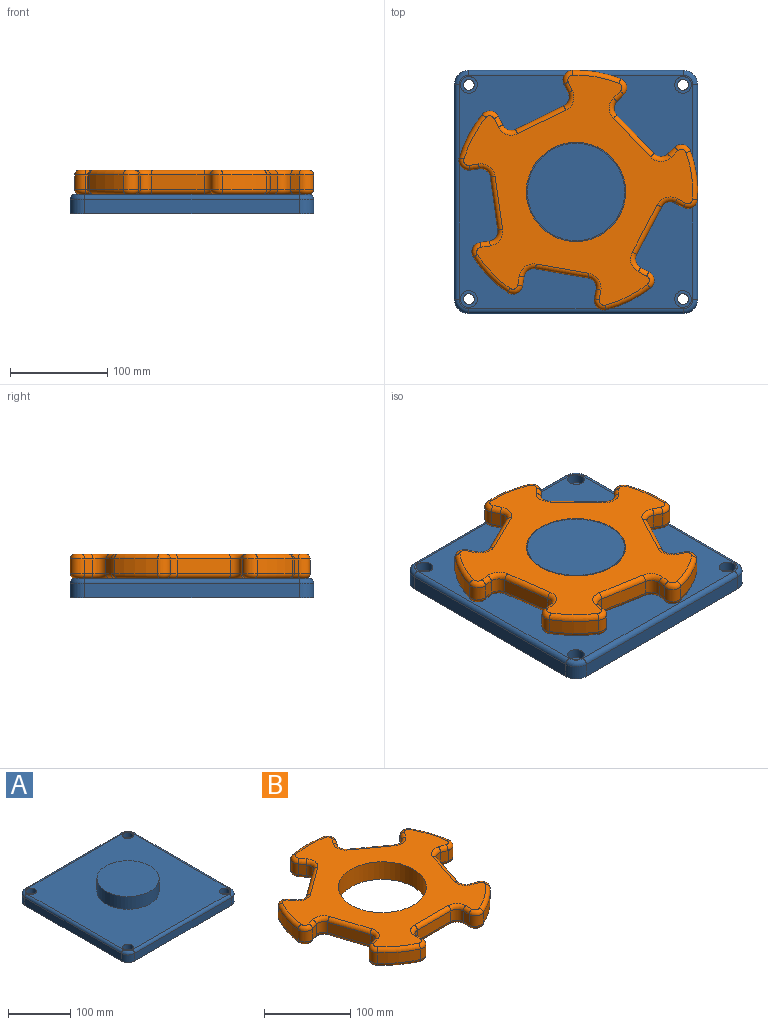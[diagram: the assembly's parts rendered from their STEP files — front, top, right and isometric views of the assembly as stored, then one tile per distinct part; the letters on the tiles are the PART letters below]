
ASSEMBLY  parts=2 mates=1
PART A: 32 faces, bbox 252.5x252.5x45 mm
  f0: plane 220x15mm, normal (1,0,0), area 3300mm2, adj f5,f8,f11,f27
  f1: plane 220x15mm, normal (0,1,0), area 3300mm2, adj f5,f8,f9,f31
  f2: plane 220x15mm, normal (-1,0,0), area 3300mm2, adj f5,f9,f10,f28
  f3: plane 220x15mm, normal (0,-1,0), area 3300mm2, adj f5,f10,f11,f24
  f4: plane 240x240mm, normal (0,0,1), area 48725.4mm2, adj f6,f14,f17,f20,f23,f24,f25,f26
  f5: plane 250x250mm, normal (0,0,-1), area 61926.7mm2, adj f0,f1,f2,f3,f8,f9,f10,f11
  f6: cylinder r=50mm len=100mm, axis (0,0,-1), area 7854mm2, adj f4,f7
  f7: plane 100x100mm, normal (0,0,1), area 7854mm2, adj f6
  f8: cylinder r=15mm len=15mm, axis (0,0,-1), area 353.4mm2, adj f0,f1,f5,f29
  f9: cylinder r=15mm len=15mm, axis (0,0,1), area 353.4mm2, adj f1,f2,f5,f30
  f10: cylinder r=15mm len=15mm, axis (0,0,-1), area 353.4mm2, adj f2,f3,f5,f26
  f11: cylinder r=15mm len=15mm, axis (0,0,1), area 353.4mm2, adj f0,f3,f5,f25
  f12: cylinder r=5.5mm len=11mm, axis (0,0,1), area 345.6mm2, adj f5,f13
  f13: plane 17.25x17.25mm, normal (0,0,1), area 138.7mm2, adj f12,f14
  f14: cylinder r=8.62mm len=17.25mm, axis (0,0,1), area 541.9mm2, adj f4,f13
  f15: cylinder r=5.5mm len=11mm, axis (0,0,1), area 345.6mm2, adj f5,f16
  f16: plane 17.25x17.25mm, normal (0,0,1), area 138.7mm2, adj f15,f17
  f17: cylinder r=8.62mm len=17.25mm, axis (0,0,1), area 541.9mm2, adj f4,f16
  f18: cylinder r=5.5mm len=11mm, axis (0,0,1), area 345.6mm2, adj f5,f19
  f19: plane 17.25x17.25mm, normal (0,0,1), area 138.7mm2, adj f18,f20
  f20: cylinder r=8.62mm len=17.25mm, axis (0,0,1), area 541.9mm2, adj f4,f19
  f21: cylinder r=5.5mm len=11mm, axis (0,0,1), area 345.6mm2, adj f5,f22
  f22: plane 17.25x17.25mm, normal (0,0,1), area 138.7mm2, adj f21,f23
  f23: cylinder r=8.62mm len=17.25mm, axis (0,0,1), area 541.9mm2, adj f4,f22
  f24: cylinder r=5mm len=220mm, axis (-1,0,0), area 1727.9mm2, adj f3,f4,f25,f26
  f25: torus R=10mm, axis (0,0,1), area 162.6mm2, adj f4,f11,f24,f27
  f26: torus R=10mm, axis (0,0,1), area 162.6mm2, adj f4,f10,f24,f28
  f27: cylinder r=5mm len=220mm, axis (0,-1,0), area 1727.9mm2, adj f0,f4,f25,f29
  f28: cylinder r=5mm len=220mm, axis (0,1,0), area 1727.9mm2, adj f2,f4,f26,f30
  f29: torus R=10mm, axis (0,0,1), area 162.6mm2, adj f4,f8,f27,f31
  f30: torus R=10mm, axis (0,0,1), area 162.6mm2, adj f4,f9,f28,f31
  f31: cylinder r=5mm len=220mm, axis (1,0,0), area 1727.9mm2, adj f1,f4,f29,f30
PART B: 123 faces, bbox 268.9x258.5x25 mm
  f0: plane 238.57x229.73mm, normal (0,0,1), area 21505.7mm2, adj f6,f83,f84,f85,f86,f87,f88,f89
  f1: plane 238.57x229.73mm, normal (0,0,-1), area 21505.7mm2, adj f6,f43,f44,f45,f46,f47,f48,f49
  f2: cylinder r=125mm len=47.82mm, axis (0,0,-1), area 759.5mm2, adj f34,f42,f74,f114
  f3: cylinder r=125mm len=50.29mm, axis (0,0,-1), area 759.5mm2, adj f27,f35,f75,f115
  f4: cylinder r=125mm len=47.82mm, axis (0,0,-1), area 759.5mm2, adj f20,f28,f59,f99
  f5: cylinder r=125mm len=40.68mm, axis (0,0,-1), area 759.5mm2, adj f13,f21,f43,f83
  f6: cylinder r=51mm len=102mm, axis (0,0,-1), area 8011.1mm2, adj f0,f1
  f7: cylinder r=125mm len=40.68mm, axis (0,0,-1), area 759.5mm2, adj f14,f41,f58,f98
  f8: plane 15x9.73mm, normal (-1,0,0), area 146mm2, adj f11,f14,f54,f94
  f9: plane 55x15mm, normal (0,-1,0), area 825mm2, adj f11,f12,f50,f90
  f10: plane 15x9.73mm, normal (1,0,0), area 146mm2, adj f12,f13,f46,f86
  f11: cylinder r=10mm len=15mm, axis (0,0,-1), area 235.6mm2, adj f8,f9,f52,f92
  f12: cylinder r=10mm len=15mm, axis (0,0,-1), area 235.6mm2, adj f9,f10,f48,f88
  f13: cylinder r=10mm len=15mm, axis (0,0,-1), area 299.5mm2, adj f5,f10,f44,f84
  f14: cylinder r=10mm len=15mm, axis (0,0,-1), area 299.5mm2, adj f7,f8,f56,f96
  f15: plane 15x9.26mm, normal (-0.31,0.95,0), area 146mm2, adj f18,f21,f47,f87
  f16: plane 52.31x17mm, normal (-0.95,-0.31,0), area 825mm2, adj f18,f19,f51,f91
  f17: plane 15x9.26mm, normal (0.31,-0.95,0), area 146mm2, adj f19,f20,f55,f95
  f18: cylinder r=10mm len=15mm, axis (0,0,-1), area 235.6mm2, adj f15,f16,f49,f89
  f19: cylinder r=10mm len=15mm, axis (0,0,-1), area 235.6mm2, adj f16,f17,f53,f93
  f20: cylinder r=10mm len=15mm, axis (0,0,-1), area 299.5mm2, adj f4,f17,f57,f97
  f21: cylinder r=10mm len=16.25mm, axis (0,0,-1), area 299.5mm2, adj f5,f15,f45,f85
  f22: plane 15x7.87mm, normal (0.81,0.59,0), area 146mm2, adj f25,f28,f63,f103
  f23: plane 44.5x32.33mm, normal (-0.59,0.81,0), area 825mm2, adj f25,f26,f67,f107
  f24: plane 15x7.87mm, normal (-0.81,-0.59,0), area 146mm2, adj f26,f27,f71,f111
  f25: cylinder r=10mm len=15mm, axis (0,0,-1), area 235.6mm2, adj f22,f23,f65,f105
  f26: cylinder r=10mm len=15mm, axis (0,0,-1), area 235.6mm2, adj f23,f24,f69,f109
  f27: cylinder r=10mm len=15.67mm, axis (0,0,-1), area 299.5mm2, adj f3,f24,f73,f113
  f28: cylinder r=10mm len=16.78mm, axis (0,0,-1), area 299.5mm2, adj f4,f22,f61,f101
  f29: plane 15x7.87mm, normal (0.81,-0.59,0), area 146mm2, adj f32,f35,f79,f119
  f30: plane 44.5x32.33mm, normal (0.59,0.81,0), area 825mm2, adj f32,f33,f82,f122
  f31: plane 15x7.87mm, normal (-0.81,0.59,0), area 146mm2, adj f33,f34,f78,f118
  f32: cylinder r=10mm len=15mm, axis (0,0,-1), area 235.6mm2, adj f29,f30,f81,f121
  f33: cylinder r=10mm len=15mm, axis (0,0,-1), area 235.6mm2, adj f30,f31,f80,f120
  f34: cylinder r=10mm len=16.78mm, axis (0,0,-1), area 299.5mm2, adj f2,f31,f76,f116
  f35: cylinder r=10mm len=15.67mm, axis (0,0,-1), area 299.5mm2, adj f3,f29,f77,f117
  f36: plane 15x9.26mm, normal (-0.31,-0.95,0), area 146mm2, adj f39,f42,f70,f110
  f37: plane 52.31x17mm, normal (0.95,-0.31,0), area 825mm2, adj f39,f40,f66,f106
  f38: plane 15x9.26mm, normal (0.31,0.95,0), area 146mm2, adj f40,f41,f62,f102
  f39: cylinder r=10mm len=15mm, axis (0,0,-1), area 235.6mm2, adj f36,f37,f68,f108
  f40: cylinder r=10mm len=15mm, axis (0,0,-1), area 235.6mm2, adj f37,f38,f64,f104
  f41: cylinder r=10mm len=16.25mm, axis (0,0,-1), area 299.5mm2, adj f7,f38,f60,f100
  f42: cylinder r=10mm len=15mm, axis (0,0,-1), area 299.5mm2, adj f2,f36,f72,f112
  f43: torus R=120mm, axis (0,0,1), area 391.9mm2, adj f1,f5,f44,f45
  f44: torus R=5mm, axis (0,0,1), area 128.3mm2, adj f1,f13,f43,f46
  f45: torus R=5mm, axis (0,0,1), area 128.3mm2, adj f1,f21,f43,f47
  f46: cylinder r=5mm len=9.73mm, axis (0,-1,0), area 76.4mm2, adj f1,f10,f44,f48
  f47: cylinder r=5mm len=10.8mm, axis (0.95,0.31,0), area 76.4mm2, adj f1,f15,f45,f49
  f48: torus R=15mm, axis (0,0,1), area 145.8mm2, adj f1,f12,f46,f50
  f49: torus R=15mm, axis (0,0,1), area 145.8mm2, adj f1,f18,f47,f51
  f50: cylinder r=5mm len=55mm, axis (-1,0,0), area 432mm2, adj f1,f9,f48,f52
  f51: cylinder r=5mm len=53.85mm, axis (-0.31,0.95,0), area 432mm2, adj f1,f16,f49,f53
  f52: torus R=15mm, axis (0,0,1), area 145.8mm2, adj f1,f11,f50,f54
  f53: torus R=15mm, axis (0,0,1), area 145.8mm2, adj f1,f19,f51,f55
  f54: cylinder r=5mm len=9.73mm, axis (0,1,0), area 76.4mm2, adj f1,f8,f52,f56
  f55: cylinder r=5mm len=10.8mm, axis (-0.95,-0.31,0), area 76.4mm2, adj f1,f17,f53,f57
  f56: torus R=5mm, axis (0,0,1), area 128.3mm2, adj f1,f14,f54,f58
  f57: torus R=5mm, axis (0,0,1), area 128.3mm2, adj f1,f20,f55,f59
  f58: torus R=120mm, axis (0,0,1), area 391.9mm2, adj f1,f7,f56,f60
  f59: torus R=120mm, axis (0,0,1), area 391.9mm2, adj f1,f4,f57,f61
  f60: torus R=5mm, axis (0,0,1), area 128.3mm2, adj f1,f41,f58,f62
  f61: torus R=5mm, axis (0,0,1), area 128.3mm2, adj f1,f28,f59,f63
  f62: cylinder r=5mm len=10.8mm, axis (0.95,-0.31,0), area 76.4mm2, adj f1,f38,f60,f64
  f63: cylinder r=5mm len=10.81mm, axis (0.59,-0.81,0), area 76.4mm2, adj f1,f22,f61,f65
  f64: torus R=15mm, axis (0,0,1), area 145.8mm2, adj f1,f40,f62,f66
  f65: torus R=15mm, axis (0,0,1), area 145.8mm2, adj f1,f25,f63,f67
  f66: cylinder r=5mm len=53.85mm, axis (-0.31,-0.95,0), area 432mm2, adj f1,f37,f64,f68
  f67: cylinder r=5mm len=47.44mm, axis (0.81,0.59,0), area 432mm2, adj f1,f23,f65,f69
  f68: torus R=15mm, axis (0,0,1), area 145.8mm2, adj f1,f39,f66,f70
  f69: torus R=15mm, axis (0,0,1), area 145.8mm2, adj f1,f26,f67,f71
  f70: cylinder r=5mm len=10.8mm, axis (-0.95,0.31,0), area 76.4mm2, adj f1,f36,f68,f72
  f71: cylinder r=5mm len=10.81mm, axis (-0.59,0.81,0), area 76.4mm2, adj f1,f24,f69,f73
  f72: torus R=5mm, axis (0,0,1), area 128.3mm2, adj f1,f42,f70,f74
  f73: torus R=5mm, axis (0,0,1), area 128.3mm2, adj f1,f27,f71,f75
  f74: torus R=120mm, axis (0,0,1), area 391.9mm2, adj f1,f2,f72,f76
  f75: torus R=120mm, axis (0,0,1), area 391.9mm2, adj f1,f3,f73,f77
  f76: torus R=5mm, axis (0,0,1), area 128.3mm2, adj f1,f34,f74,f78
  f77: torus R=5mm, axis (0,0,1), area 128.3mm2, adj f1,f35,f75,f79
  f78: cylinder r=5mm len=10.81mm, axis (0.59,0.81,0), area 76.4mm2, adj f1,f31,f76,f80
  f79: cylinder r=5mm len=10.81mm, axis (-0.59,-0.81,0), area 76.4mm2, adj f1,f29,f77,f81
  f80: torus R=15mm, axis (0,0,1), area 145.8mm2, adj f1,f33,f78,f82
  f81: torus R=15mm, axis (0,0,1), area 145.8mm2, adj f1,f32,f79,f82
  f82: cylinder r=5mm len=47.44mm, axis (0.81,-0.59,0), area 432mm2, adj f1,f30,f80,f81
  f83: torus R=120mm, axis (0,0,1), area 391.9mm2, adj f0,f5,f84,f85
  f84: torus R=5mm, axis (0,0,1), area 128.3mm2, adj f0,f13,f83,f86
  f85: torus R=5mm, axis (0,0,1), area 128.3mm2, adj f0,f21,f83,f87
  f86: cylinder r=5mm len=9.73mm, axis (0,1,0), area 76.4mm2, adj f0,f10,f84,f88
  f87: cylinder r=5mm len=10.8mm, axis (-0.95,-0.31,0), area 76.4mm2, adj f0,f15,f85,f89
  f88: torus R=15mm, axis (0,0,1), area 145.8mm2, adj f0,f12,f86,f90
  f89: torus R=15mm, axis (0,0,1), area 145.8mm2, adj f0,f18,f87,f91
  f90: cylinder r=5mm len=55mm, axis (1,0,0), area 432mm2, adj f0,f9,f88,f92
  f91: cylinder r=5mm len=53.85mm, axis (0.31,-0.95,0), area 432mm2, adj f0,f16,f89,f93
  f92: torus R=15mm, axis (0,0,1), area 145.8mm2, adj f0,f11,f90,f94
  f93: torus R=15mm, axis (0,0,1), area 145.8mm2, adj f0,f19,f91,f95
  f94: cylinder r=5mm len=9.73mm, axis (0,-1,0), area 76.4mm2, adj f0,f8,f92,f96
  f95: cylinder r=5mm len=10.8mm, axis (0.95,0.31,0), area 76.4mm2, adj f0,f17,f93,f97
  f96: torus R=5mm, axis (0,0,1), area 128.3mm2, adj f0,f14,f94,f98
  f97: torus R=5mm, axis (0,0,1), area 128.3mm2, adj f0,f20,f95,f99
  f98: torus R=120mm, axis (0,0,1), area 391.9mm2, adj f0,f7,f96,f100
  f99: torus R=120mm, axis (0,0,1), area 391.9mm2, adj f0,f4,f97,f101
  f100: torus R=5mm, axis (0,0,1), area 128.3mm2, adj f0,f41,f98,f102
  f101: torus R=5mm, axis (0,0,1), area 128.3mm2, adj f0,f28,f99,f103
  f102: cylinder r=5mm len=10.8mm, axis (-0.95,0.31,0), area 76.4mm2, adj f0,f38,f100,f104
  f103: cylinder r=5mm len=10.81mm, axis (-0.59,0.81,0), area 76.4mm2, adj f0,f22,f101,f105
  f104: torus R=15mm, axis (0,0,1), area 145.8mm2, adj f0,f40,f102,f106
  f105: torus R=15mm, axis (0,0,1), area 145.8mm2, adj f0,f25,f103,f107
  f106: cylinder r=5mm len=53.85mm, axis (0.31,0.95,0), area 432mm2, adj f0,f37,f104,f108
  f107: cylinder r=5mm len=47.44mm, axis (-0.81,-0.59,0), area 432mm2, adj f0,f23,f105,f109
  f108: torus R=15mm, axis (0,0,1), area 145.8mm2, adj f0,f39,f106,f110
  f109: torus R=15mm, axis (0,0,1), area 145.8mm2, adj f0,f26,f107,f111
  f110: cylinder r=5mm len=10.8mm, axis (0.95,-0.31,0), area 76.4mm2, adj f0,f36,f108,f112
  f111: cylinder r=5mm len=10.81mm, axis (0.59,-0.81,0), area 76.4mm2, adj f0,f24,f109,f113
  f112: torus R=5mm, axis (0,0,1), area 128.3mm2, adj f0,f42,f110,f114
  f113: torus R=5mm, axis (0,0,1), area 128.3mm2, adj f0,f27,f111,f115
  f114: torus R=120mm, axis (0,0,1), area 391.9mm2, adj f0,f2,f112,f116
  f115: torus R=120mm, axis (0,0,1), area 391.9mm2, adj f0,f3,f113,f117
  f116: torus R=5mm, axis (0,0,1), area 128.3mm2, adj f0,f34,f114,f118
  f117: torus R=5mm, axis (0,0,1), area 128.3mm2, adj f0,f35,f115,f119
  f118: cylinder r=5mm len=10.81mm, axis (-0.59,-0.81,0), area 76.4mm2, adj f0,f31,f116,f120
  f119: cylinder r=5mm len=10.81mm, axis (0.59,0.81,0), area 76.4mm2, adj f0,f29,f117,f121
  f120: torus R=15mm, axis (0,0,1), area 145.8mm2, adj f0,f33,f118,f122
  f121: torus R=15mm, axis (0,0,1), area 145.8mm2, adj f0,f32,f119,f122
  f122: cylinder r=5mm len=47.44mm, axis (-0.81,0.59,0), area 432mm2, adj f0,f30,f120,f121
PLACE A at identity fixed
PLACE B rot(axis=(0,0,-1),153.9deg) t=(0,0,0)mm
MATE revolute B.f2 <-> A.f6  axis (0,0,-1) through (0,0,45)mm
